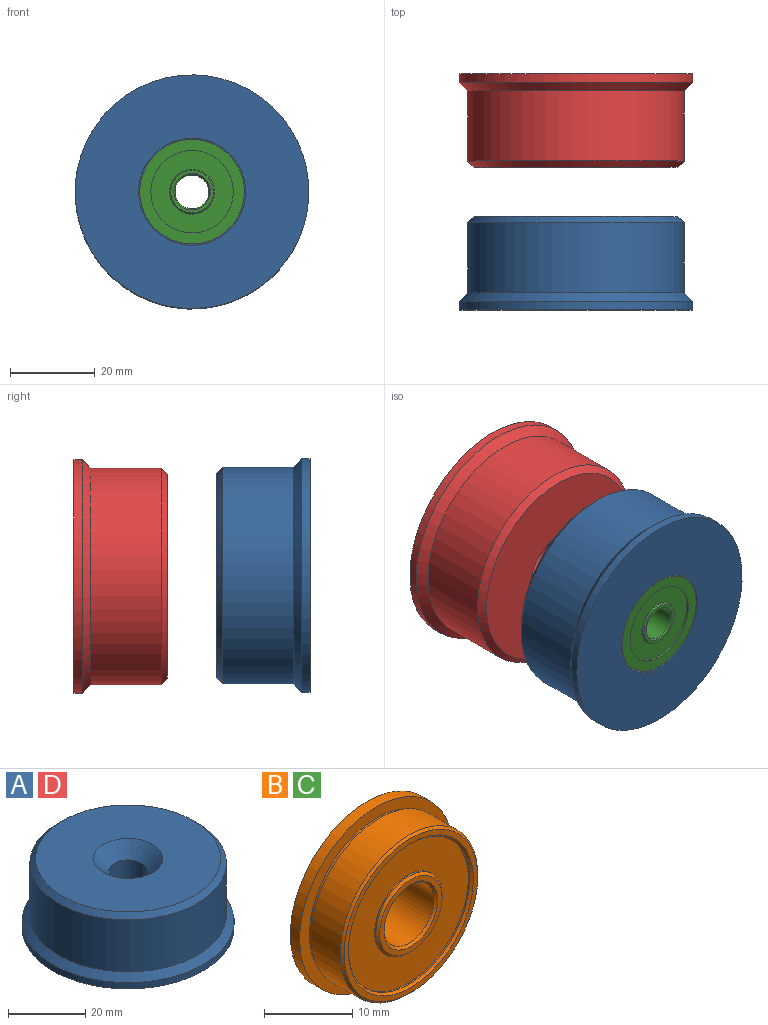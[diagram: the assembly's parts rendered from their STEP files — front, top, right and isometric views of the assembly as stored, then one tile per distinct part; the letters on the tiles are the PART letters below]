
ASSEMBLY  parts=4 mates=1
PART A: 12 faces, bbox 55x55x22 mm
  f0: plane 55x55mm, normal (0,0,-1), area 1877.1mm2, adj f3,f8
  f1: cylinder r=5mm len=10.9mm, axis (0,0,-1), area 342.4mm2, adj f6,f10
  f2: plane 48x48mm, normal (0,0,1), area 1555.1mm2, adj f10,f11
  f3: cylinder r=12.6mm len=25.2mm, axis (0,0,-1), area 126.7mm2, adj f0,f4
  f4: plane 25.2x25.2mm, normal (0,0,-1), area 115.2mm2, adj f3,f5
  f5: cylinder r=11.05mm len=22.1mm, axis (0,0,-1), area 381.9mm2, adj f4,f6
  f6: plane 22.1x22.1mm, normal (0,0,-1), area 305.1mm2, adj f1,f5
  f7: cylinder r=25.5mm len=51mm, axis (0,0,-1), area 2643.7mm2, adj f9,f11
  f8: cylinder r=27.5mm len=55mm, axis (0,0,-1), area 345.6mm2, adj f0,f9
  f9: cone r=25.5mm half-angle=45deg, axis (0,0,-1), area 470.9mm2, adj f7,f8
  f10: cone r=5mm half-angle=45deg, axis (0,0,1), area 248.8mm2, adj f1,f2
  f11: cone r=24mm half-angle=45deg, axis (0,0,-1), area 329.9mm2, adj f2,f7
PART B: 22 faces, bbox 24.6x7x24.6 mm
  f0: cylinder r=9.7mm len=19.4mm, axis (0,1,0), area 12.2mm2, adj f1,f18
  f1: plane 19.4x19.4mm, normal (0,-1,0), area 207.3mm2, adj f0,f2
  f2: cylinder r=5.3mm len=10.6mm, axis (0,1,0), area 6.7mm2, adj f1,f20
  f3: plane 10x10mm, normal (0,-1,0), area 20.5mm2, adj f20,f21
  f4: cylinder r=4mm len=8mm, axis (0,1,0), area 160.8mm2, adj f17,f21
  f5: plane 10x10mm, normal (0,1,0), area 20.5mm2, adj f16,f17
  f6: cylinder r=5.3mm len=10.6mm, axis (0,1,0), area 6.7mm2, adj f7,f16
  f7: plane 19.4x19.4mm, normal (0,1,0), area 207.3mm2, adj f6,f8
  f8: cylinder r=9.7mm len=19.4mm, axis (0,1,0), area 30.5mm2, adj f7,f9
  f9: plane 24.6x24.6mm, normal (0,1,0), area 179.7mm2, adj f8,f10
  f10: cylinder r=12.3mm len=24.6mm, axis (0,1,0), area 115.9mm2, adj f9,f11
  f11: plane 24.6x24.6mm, normal (0,-1,0), area 112.2mm2, adj f10,f12
  f12: cylinder r=10.75mm len=21.5mm, axis (0,1,0), area 33.8mm2, adj f11,f13
  f13: plane 22x22mm, normal (0,1,0), area 17.1mm2, adj f12,f14
  f14: cylinder r=11mm len=22mm, axis (0,1,0), area 324.8mm2, adj f13,f19
  f15: plane 21.4x21.4mm, normal (0,-1,0), area 45.5mm2, adj f18,f19
  f16: cone r=5mm half-angle=45deg, axis (0,-1,0), area 13.7mm2, adj f5,f6
  f17: cone r=4mm half-angle=45deg, axis (0,1,0), area 11.1mm2, adj f4,f5
  f18: cone r=10mm half-angle=45deg, axis (0,-1,0), area 26.3mm2, adj f0,f15
  f19: cone r=11mm half-angle=45deg, axis (0,1,0), area 28.9mm2, adj f14,f15
  f20: cone r=5.3mm half-angle=45deg, axis (0,1,0), area 13.7mm2, adj f2,f3
  f21: cone r=4.3mm half-angle=45deg, axis (0,-1,0), area 11.1mm2, adj f3,f4
PART C: same geometry as B
PART D: same geometry as A
PLACE A rot(axis=(0,0.71,0.71),179.6deg) t=(19.03,-42.11,6.79)mm
PLACE B t=(18.98,9.55,6.63)mm
PLACE C rot(axis=(-0.01,0,1),180deg) t=(19.03,-38.51,6.79)mm
PLACE D rot(axis=(1,0,0),90deg) t=(18.98,13.45,6.63)mm
MATE slider A.f1 <-> C.f0  axis (0,-1,0) through (19.03,-35.01,6.79)mm
